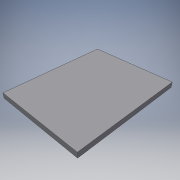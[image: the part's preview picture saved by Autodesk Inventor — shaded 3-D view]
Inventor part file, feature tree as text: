
AUTODESK INVENTOR PART (.ipt)
format: ipt  version: 2016 (Build 200138000, 138)  size: 86,528 bytes
history: native  units: in
note: dims shown in document units (in); Inventor stores cm internally (conversion verified against a paired STEP export)
features: extrude x1, sketch x1
ambient origin geometry x8: Origin, YZ Plane, XZ Plane, XY Plane, X Axis, Y Axis, Z Axis, Center Point
bodies: Solid1 (feature_tree)
feature tree (2):
  extrude  "Extrusion1"  Depth=20.0in
  sketch  "Sketch1"  dims[d0=16.0in d1=20.0in d2=1.0in d3=0.0in]
